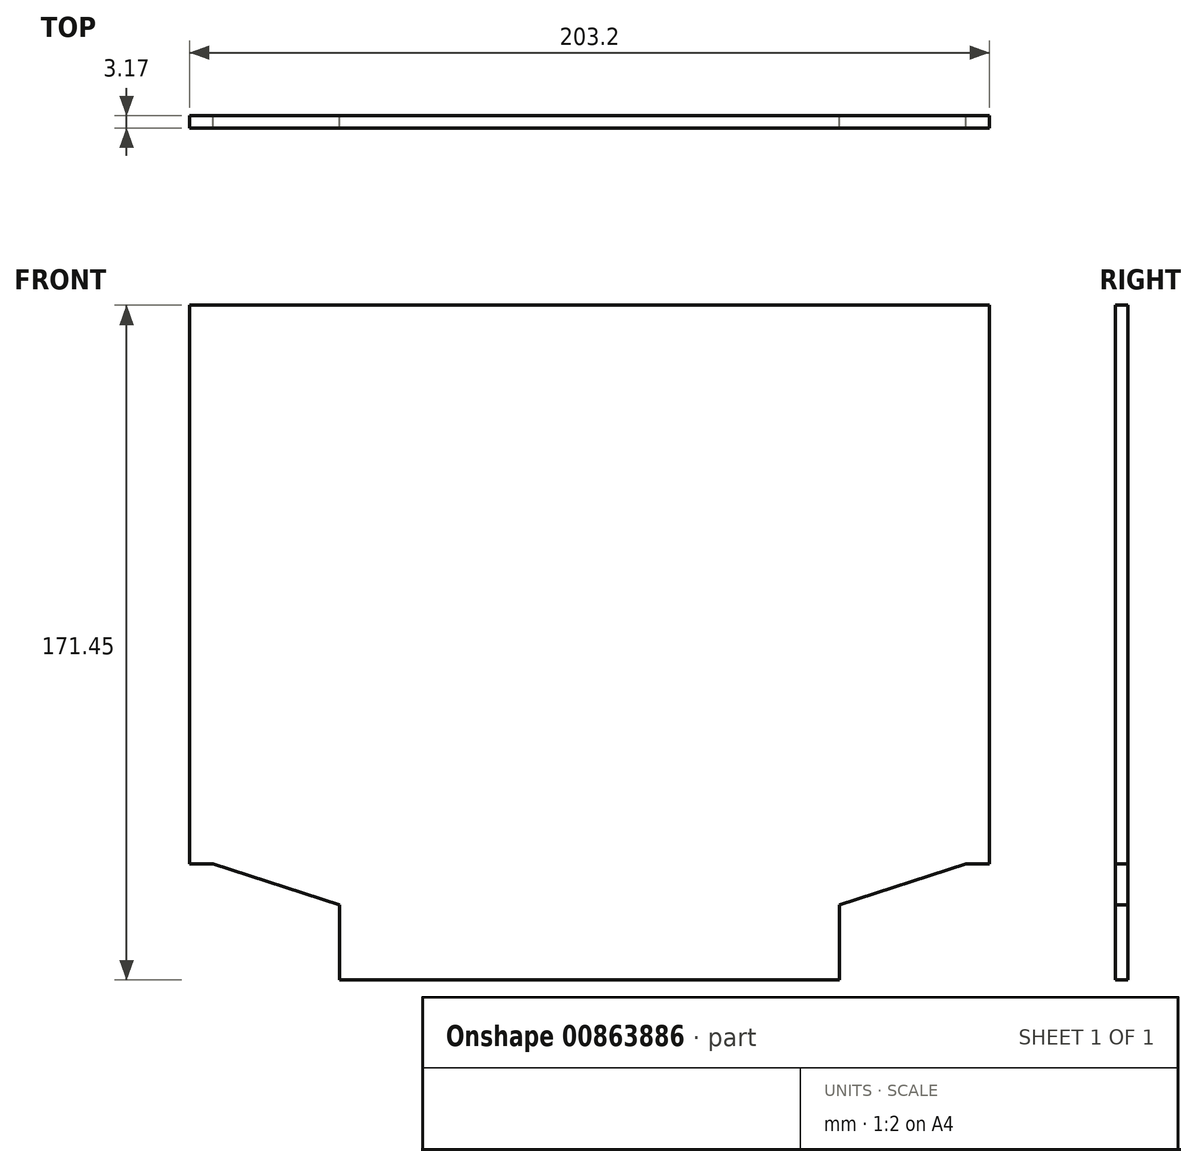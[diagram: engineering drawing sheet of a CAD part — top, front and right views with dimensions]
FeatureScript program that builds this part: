
annotation { "Feature Type Name" : "Feature", "Feature Type Description" : "" }
export const myFeature = defineFeature(function(context is Context, id is Id, definition is map)
    precondition{}
    {
        {
            var Q0;
            Q0=qCreatedBy(makeId("Front.planeOp"),FACE);
            var sketch = newSketch(context, id + "F0", { "sketchPlane" : qUnion([Q0])});
            skLineSegment(sketch, "E0", {"start": v(0, -67.75) * mm, "end": v(-63.5, -67.75) * mm});
            skLineSegment(sketch, "E1", {"start": v(-63.5, -67.75) * mm, "end": v(-63.5, -48.7) * mm});
            skLineSegment(sketch, "E2", {"start": v(-95.69, 103.7) * mm, "end": v(82.6, 103.7) * mm, "construction": true});
            skLineSegment(sketch, "E3", {"start": v(-63.5, -48.7) * mm, "end": v(-95.59, -38.28) * mm});
            skLineSegment(sketch, "E4", {"start": v(-95.59, -38.28) * mm, "end": v(-101.6, -38.28) * mm});
            skLineSegment(sketch, "E5", {"start": v(-101.6, -38.28) * mm, "end": v(-101.6, 103.7) * mm});
            skLineSegment(sketch, "E6", {"start": v(-101.6, 103.7) * mm, "end": v(0, 103.7) * mm});
            skLineSegment(sketch, "E7.MirrorCS", {"start": v(101.6, 103.7) * mm, "end": v(0, 103.7) * mm});
            skLineSegment(sketch, "E8.MirrorCS", {"start": v(63.5, -67.75) * mm, "end": v(63.5, -48.7) * mm});
            skLineSegment(sketch, "E9.MirrorCS", {"start": v(95.69, 103.7) * mm, "end": v(-82.6, 103.7) * mm, "construction": true});
            skLineSegment(sketch, "E10.MirrorCS", {"start": v(101.6, -38.28) * mm, "end": v(101.6, 103.7) * mm});
            skLineSegment(sketch, "E11.MirrorCS", {"start": v(0, -67.75) * mm, "end": v(63.5, -67.75) * mm});
            skLineSegment(sketch, "E12.MirrorCS", {"start": v(95.59, -38.28) * mm, "end": v(101.6, -38.28) * mm});
            skLineSegment(sketch, "E13.MirrorCS", {"start": v(63.5, -48.7) * mm, "end": v(95.59, -38.28) * mm});
            skSolve(sketch);
        }
        {
            var Q0;
            Q0=makeQuery(id+"F0.imprint","IMPRINT",FACE,{"disambiguationData":[TD([[makeQuery(id+"F0.imprint","IMPRINT",EDGE,{"derivedFrom":sQuery(id+"F0.wireOp",EDGE,"E0")}),-1.0]])]});
            extrude(context, id + "F1", {"entities" : qUnion([Q0]), "depth" : 3.17 * mm, "offsetDistance" : 25.4 * mm});
        }
    });
